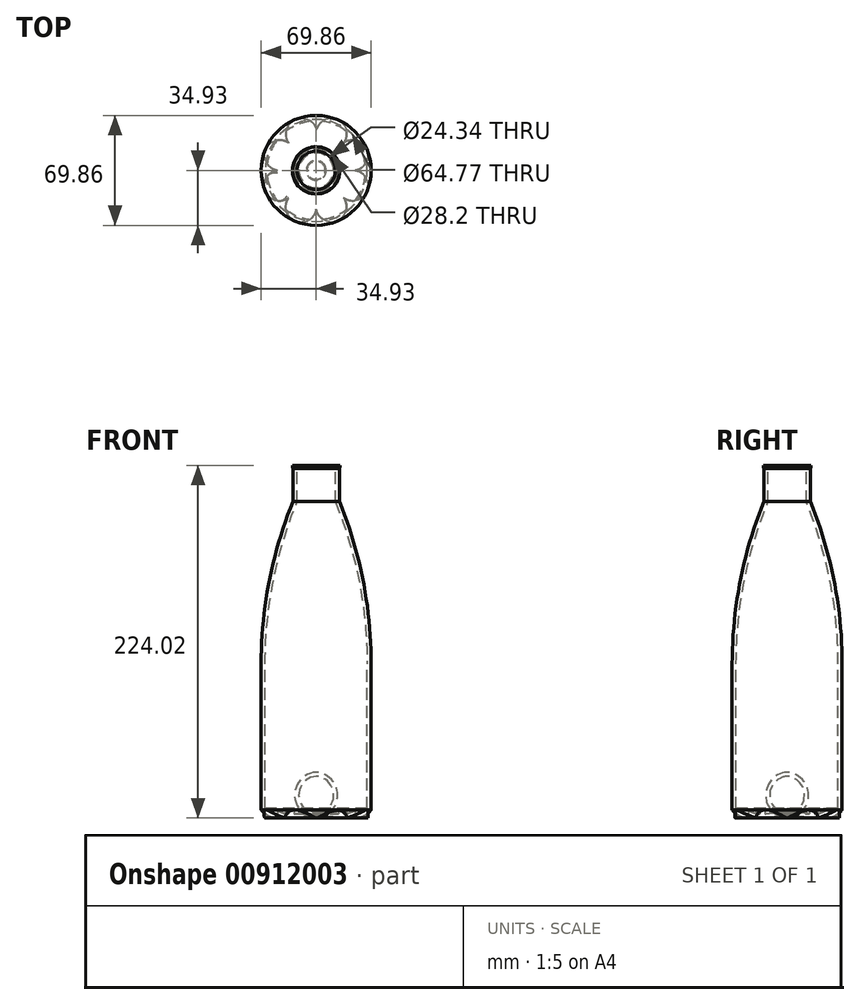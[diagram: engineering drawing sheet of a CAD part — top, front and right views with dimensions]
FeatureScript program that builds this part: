
annotation { "Feature Type Name" : "Feature", "Feature Type Description" : "" }
export const myFeature = defineFeature(function(context is Context, id is Id, definition is map)
    precondition{}
    {
        {
            var Q0;
            Q0=qCreatedBy(makeId("Front.planeOp"),FACE);
            var sketch = newSketch(context, id + "F0", { "sketchPlane" : qUnion([Q0])});
            skLineSegment(sketch, "E0", {"start": v(-34.93, -35.35) * mm, "end": v(-34.92, -128) * mm});
            skPoint(sketch, "E1.visualSharp", {"position": v(-34.92, -108.62) * mm});
            skPoint(sketch, "E2.visualSharp", {"position": v(34.92, -108.62) * mm});
            skLineSegment(sketch, "E3", {"start": v(-14.7, 68) * mm, "end": v(-14.7, 88.82) * mm});
            skArc(sketch, "E4", {"start": v(-14.97, 90.77) * mm, "mid": v(-15.09, 89.76) * mm, "end": v(-14.7, 88.82) * mm});
            skArc(sketch, "E5.MirrorCS", {"start": v(14.97, 90.77) * mm, "mid": v(15.09, 89.76) * mm, "end": v(14.7, 88.82) * mm});
            skLineSegment(sketch, "E6", {"start": v(0, 90.43) * mm, "end": v(0, -133.21) * mm, "construction": true});
            skLineSegment(sketch, "E7", {"start": v(0, 90.43) * mm, "end": v(0, -133.21) * mm});
            skLineSegment(sketch, "E8", {"start": v(-14.97, 90.77) * mm, "end": v(0, 90.43) * mm});
            skArc(sketch, "E9", {"start": v(-14.7, 68) * mm, "mid": v(-29.82, 17.3) * mm, "end": v(-34.92, -35.35) * mm});
            skArc(sketch, "E10", {"start": v(-34.92, -128) * mm, "mid": v(-30.43, -131.83) * mm, "end": v(-24.67, -133.21) * mm});
            skLineSegment(sketch, "E11", {"start": v(-24.67, -133.21) * mm, "end": v(-14.1, -133.21) * mm});
            skArc(sketch, "E12", {"start": v(-6.3, -132.24) * mm, "mid": v(-10.23, -132.5) * mm, "end": v(-14.1, -133.21) * mm});
            skArc(sketch, "E13", {"start": v(-6.3, -132.24) * mm, "mid": v(-3.2, -133.07) * mm, "end": v(0, -133.21) * mm});
            skSolve(sketch);
        }
        {
            var Q0;
            Q0=makeQuery(id+"F0.imprint","IMPRINT",FACE,{"disambiguationData":[TD([[makeQuery(id+"F0.imprint","IMPRINT",EDGE,{"derivedFrom":sQuery(id+"F0.wireOp",EDGE,"E0")}),1.0]])]});
            var Q1;
            Q1=sQuery(id+"F0.wireOp",EDGE,"E7");
            revolve(context, id + "F1", {"surfaceOperationType" : NewSurfaceOperationType.NEW, "entities" : qUnion([Q0]), "axis" : qUnion([Q1]), "revolveType" : RevolveType.FULL});
        }
        {
            var Q0;
            Q0=makeQuery(id+"F1.opRevolve","SWEPT_FACE",FACE,{"disambiguationData":[OSD([sQuery(id+"F0.wireOp",EDGE,"E8")])]});
            shell(context, id + "F2", {"entities" : qUnion([Q0]), "thickness" : 2.54 * mm});
        }
        {
            var Q0;
            Q0=makeQuery(id+"F1.opRevolve","SWEPT_FACE",FACE,{"disambiguationData":[OSD([sQuery(id+"F0.wireOp",EDGE,"E11")])]});
            var sketch = newSketch(context, id + "F3", { "sketchPlane" : qUnion([Q0])});
            skArc(sketch, "E14", {"start": v(0, 24.67) * mm, "mid": v(-13.36, 32.26) * mm, "end": v(-17.45, 17.45) * mm});
            skArc(sketch, "E15", {"start": v(17.45, 17.45) * mm, "mid": v(13.26, 32) * mm, "end": v(0, 24.67) * mm});
            skArc(sketch, "E16", {"start": v(24.67, 0) * mm, "mid": v(32.29, 13.37) * mm, "end": v(17.45, 17.45) * mm});
            skArc(sketch, "E17", {"start": v(17.45, -17.45) * mm, "mid": v(32.18, -13.33) * mm, "end": v(24.67, 0) * mm});
            skArc(sketch, "E18", {"start": v(0, -24.67) * mm, "mid": v(13.38, -32.3) * mm, "end": v(17.45, -17.45) * mm});
            skArc(sketch, "E19", {"start": v(-17.45, -17.45) * mm, "mid": v(-13.6, -32.1) * mm, "end": v(0.3, -26.08) * mm});
            skArc(sketch, "E20", {"start": v(-24.67, 0) * mm, "mid": v(-32.03, -13.27) * mm, "end": v(-17.45, -17.45) * mm});
            skArc(sketch, "E21", {"start": v(-17.45, 17.45) * mm, "mid": v(-32.34, 13.4) * mm, "end": v(-24.67, 0) * mm});
            skSolve(sketch);
        }
        {
            var Q0;
            {var subQ0=sQuery(id+"F3.wireOp",EDGE,"E14");Q0=makeQuery(id+"F3.imprint","IMPRINT",FACE,{"disambiguationData":[TD([[makeQuery(id+"F3.imprint","IMPRINT",EDGE,{"derivedFrom":subQ0}),1.0]])]});}
            var Q1;
            {var subQ0=sQuery(id+"F3.wireOp",EDGE,"E15");Q1=makeQuery(id+"F3.imprint","IMPRINT",FACE,{"disambiguationData":[TD([[makeQuery(id+"F3.imprint","IMPRINT",EDGE,{"derivedFrom":subQ0}),1.0]])]});}
            var Q2;
            {var subQ0=sQuery(id+"F3.wireOp",EDGE,"E16");Q2=makeQuery(id+"F3.imprint","IMPRINT",FACE,{"disambiguationData":[TD([[makeQuery(id+"F3.imprint","IMPRINT",EDGE,{"derivedFrom":subQ0}),1.0]])]});}
            var Q3;
            {var subQ0=sQuery(id+"F3.wireOp",EDGE,"E17");Q3=makeQuery(id+"F3.imprint","IMPRINT",FACE,{"disambiguationData":[TD([[makeQuery(id+"F3.imprint","IMPRINT",EDGE,{"derivedFrom":subQ0}),1.0]])]});}
            var Q4;
            {var subQ0=sQuery(id+"F3.wireOp",EDGE,"E18");var subQ3=makeQuery(id+"F3.imprint","INTERSECT",VERTEX,{"derivedFrom":[subQ0,sQuery(id+"F3.wireOp",EDGE,"E19")]});Q4=makeQuery(id+"F3.imprint","IMPRINT",FACE,{"disambiguationData":[TD([[makeQuery(id+"F3.imprint","IMPRINT",EDGE,{"disambiguationData":[TD([[subQ3,1.0]])],"derivedFrom":subQ0}),1.0]])]});}
            var Q5;
            {var subQ3=sQuery(id+"F3.wireOp",EDGE,"E19");Q5=makeQuery(id+"F3.imprint","IMPRINT",FACE,{"disambiguationData":[TD([[makeQuery(id+"F3.imprint","IMPRINT",EDGE,{"derivedFrom":subQ3}),1.0]])]});}
            var Q6;
            {var subQ0=sQuery(id+"F3.wireOp",EDGE,"E20");Q6=makeQuery(id+"F3.imprint","IMPRINT",FACE,{"disambiguationData":[TD([[makeQuery(id+"F3.imprint","IMPRINT",EDGE,{"derivedFrom":subQ0}),1.0]])]});}
            var Q7;
            {var subQ0=sQuery(id+"F3.wireOp",EDGE,"E21");Q7=makeQuery(id+"F3.imprint","IMPRINT",FACE,{"disambiguationData":[TD([[makeQuery(id+"F3.imprint","IMPRINT",EDGE,{"derivedFrom":subQ0}),1.0]])]});}
            var Q8;
            {var subQ2=makeQuery(id+"F1.opRevolve","SWEPT_EDGE",EDGE,{"disambiguationData":[OSD([sQuery(id+"F0.wireOp",EDGE,"NignQfUM-3kd4-hX80-PKr3-ujLhkXHSJqvo"),sQuery(id+"F0.wireOp",EDGE,"E10")])]});var subQ12=sQuery(id+"F3.wireOp",EDGE,"E18");var subQ14=makeQuery(id+"F3.imprint","INTERSECT",VERTEX,{"derivedFrom":[subQ2,subQ12]});Q8=makeQuery(id+"F3.imprint","IMPRINT",FACE,{"disambiguationData":[TD([[makeQuery(id+"F3.imprint","IMPRINT",EDGE,{"disambiguationData":[TD([[subQ14,1.0]])],"derivedFrom":subQ2}),-1.0]])]});}
            extrude(context, id + "F4", {"entities" : qUnion([Q0, Q1, Q2, Q3, Q4, Q5, Q6, Q7, Q8]), "operationType" : NewBodyOperationType.ADD, "oppositeDirection" : true, "depth" : 5.08 * mm, "offsetDistance" : 25.4 * mm});
        }
        {
            var Q0;
            Q0=makeQuery(id+"F4.opExtrude","CAP_EDGE",EDGE,{"disambiguationData":[OSD([sQuery(id+"F3.wireOp",EDGE,"E21")])],"isStart":true});
            fillet(context, id + "F5", {"entities" : qUnion([Q0]), "radius" : 1.52 * mm, "tangentPropagation" : true, "allowEdgeOverflow" : false});
        }
    });
